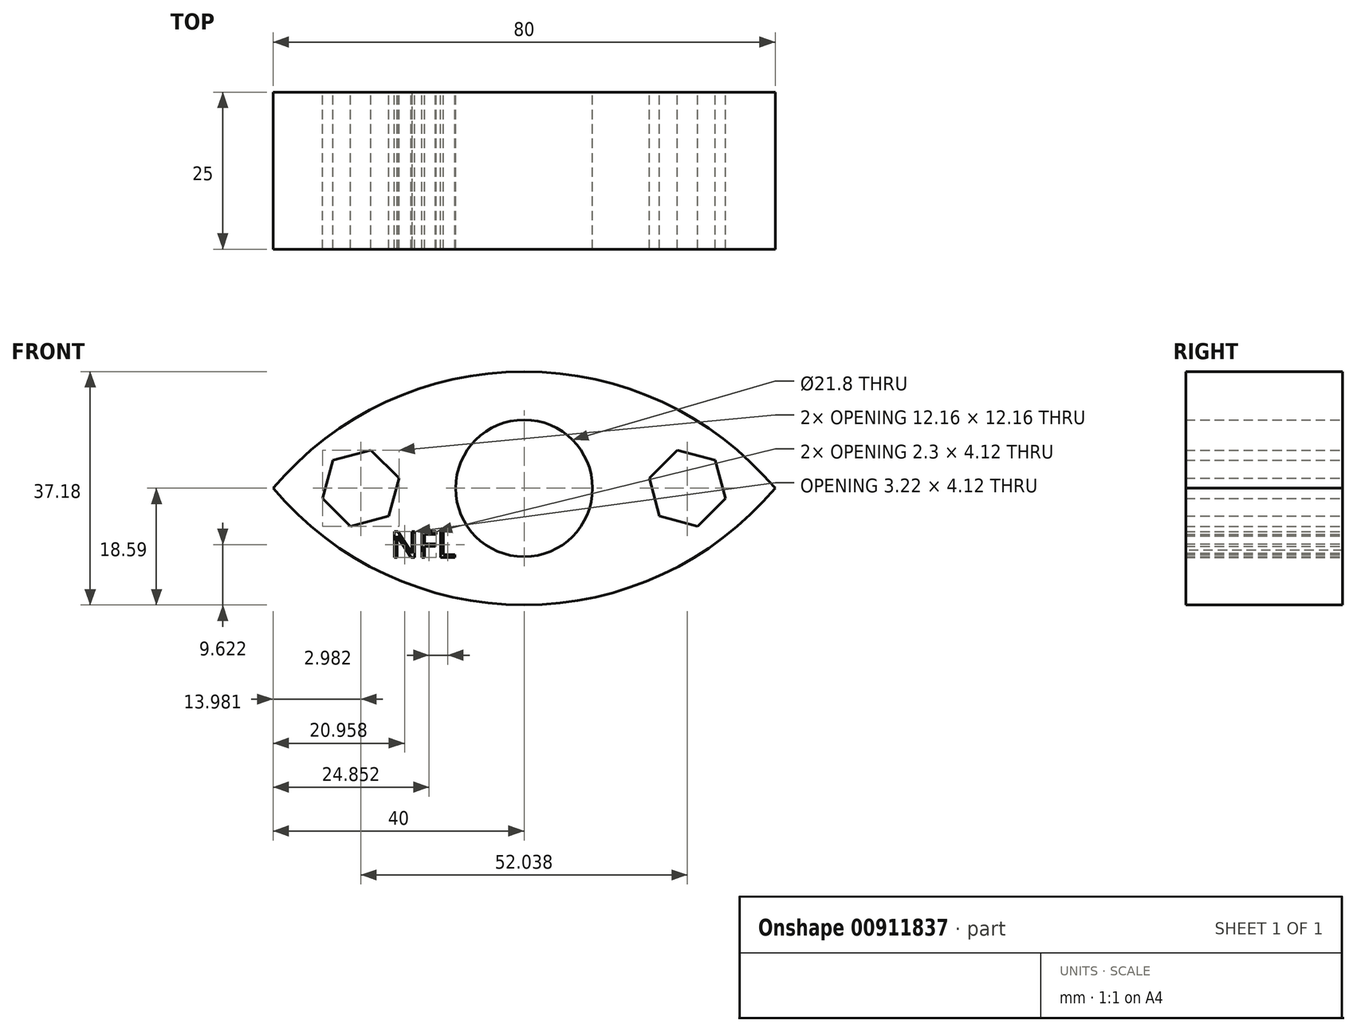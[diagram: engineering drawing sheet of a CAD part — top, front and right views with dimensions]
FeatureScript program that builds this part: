
annotation { "Feature Type Name" : "Feature", "Feature Type Description" : "" }
export const myFeature = defineFeature(function(context is Context, id is Id, definition is map)
    precondition{}
    {
        {
            var Q0;
            Q0=qCreatedBy(makeId("Front.planeOp"),FACE);
            var sketch = newSketch(context, id + "F0", { "sketchPlane" : qUnion([Q0])});
            skCircle(sketch, "E0", {"center": v(0, 0) * mm, "radius": 10.9 * mm});
            skCircle(sketch, "E1.cCircle", {"center": v(26.02, 0) * mm, "radius": 5.45 * mm, "construction": true});
            skLineSegment(sketch, "E1.0", {"start": v(27.64, -6.08) * mm, "end": v(21.57, -4.45) * mm});
            skLineSegment(sketch, "E1.1", {"start": v(21.57, -4.45) * mm, "end": v(19.94, 1.63) * mm});
            skLineSegment(sketch, "E1.2", {"start": v(19.94, 1.63) * mm, "end": v(24.4, 6.08) * mm});
            skLineSegment(sketch, "E1.3", {"start": v(24.4, 6.08) * mm, "end": v(30.47, 4.45) * mm});
            skLineSegment(sketch, "E1.4", {"start": v(30.47, 4.45) * mm, "end": v(32.1, -1.63) * mm});
            skLineSegment(sketch, "E1.5", {"start": v(32.1, -1.63) * mm, "end": v(27.64, -6.08) * mm});
            skPoint(sketch, "E1.0.midPoint", {"position": v(24.6, -5.26) * mm});
            skLineSegment(sketch, "E2.MirrorCS", {"start": v(-27.64, -6.08) * mm, "end": v(-21.57, -4.45) * mm});
            skLineSegment(sketch, "E3.MirrorCS", {"start": v(-30.47, 4.45) * mm, "end": v(-32.1, -1.63) * mm});
            skCircle(sketch, "E4.MirrorC", {"center": v(-26.02, 0) * mm, "radius": 5.45 * mm, "construction": true});
            skLineSegment(sketch, "E5.MirrorCS", {"start": v(-32.1, -1.63) * mm, "end": v(-27.64, -6.08) * mm});
            skLineSegment(sketch, "E6.MirrorCS", {"start": v(-24.4, 6.08) * mm, "end": v(-30.47, 4.45) * mm});
            skLineSegment(sketch, "E7.MirrorCS", {"start": v(-21.57, -4.45) * mm, "end": v(-19.94, 1.63) * mm});
            skPoint(sketch, "E8.MirrorP", {"position": v(-24.6, -5.26) * mm});
            skLineSegment(sketch, "E9.MirrorCS", {"start": v(-19.94, 1.63) * mm, "end": v(-24.4, 6.08) * mm});
            skText(sketch, "E10", { "text": "NFL", "fontName": "OpenSans-Regular.ttf"});
            skPoint(sketch, "E11.end.orphan", {"position": v(-55.23, 0) * mm});
            skPoint(sketch, "E11.start.orphan", {"position": v(48, 0) * mm});
            skArc(sketch, "E12", {"start": v(40, 0) * mm, "mid": v(0, 18.59) * mm, "end": v(-40, 0) * mm});
            skArc(sketch, "E13.MirrorCS", {"start": v(40, 0) * mm, "mid": v(0, -18.59) * mm, "end": v(-40, 0) * mm});
            const initialGuessF0  = {"E10": [-0.02122, -0.01103, 1, 0, 0.00416]};
            skSetInitialGuess(sketch, initialGuessF0);
            skSolve(sketch);
        }
        {
            var Q0;
            Q0=makeQuery(id+"F0.imprint","IMPRINT",FACE,{"disambiguationData":[TD([[makeQuery(id+"F0.imprint","IMPRINT",EDGE,{"derivedFrom":sQuery(id+"F0.wireOp",EDGE,"E0")}),-1.0]])]});
            extrude(context, id + "F1", {"entities" : qUnion([Q0]), "depth" : 7 * mm, "offsetDistance" : 25 * mm});
        }
        {
            var Q0;
            Q0 = qSketchRegion(id + "F0", true);
            extrude(context, id + "F2", {"entities" : qUnion([Q0]), "operationType" : NewBodyOperationType.ADD, "depth" : 25 * mm, "offsetDistance" : 25 * mm});
        }
    });
